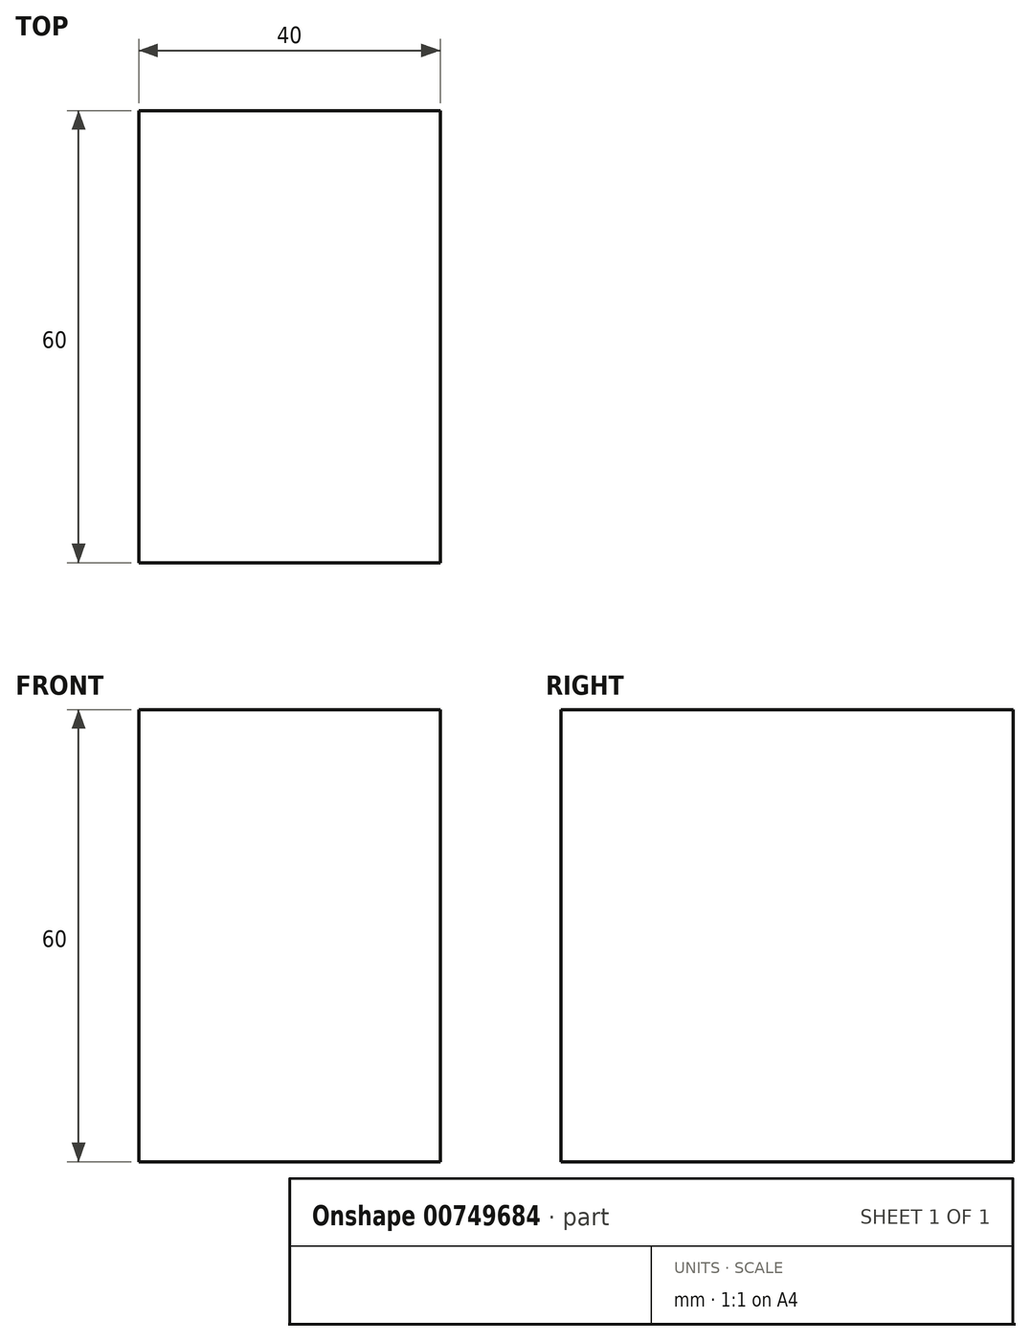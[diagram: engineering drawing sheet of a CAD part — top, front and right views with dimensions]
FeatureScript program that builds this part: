
annotation { "Feature Type Name" : "Feature", "Feature Type Description" : "" }
export const myFeature = defineFeature(function(context is Context, id is Id, definition is map)
    precondition{}
    {
        {
            var Q0;
            Q0=qCreatedBy(makeId("Front.planeOp"),FACE);
            var sketch = newSketch(context, id + "F0", { "sketchPlane" : qUnion([Q0])});
            skLineSegment(sketch, "E0", {"start": v(0, 0) * mm, "end": v(0, 60) * mm});
            skLineSegment(sketch, "E1", {"start": v(0, 60) * mm, "end": v(40, 60) * mm});
            skLineSegment(sketch, "E2", {"start": v(40, 60) * mm, "end": v(40, 0) * mm});
            skLineSegment(sketch, "E3", {"start": v(40, 0) * mm, "end": v(0, 0) * mm});
            skSolve(sketch);
        }
        {
            var Q0;
            Q0=makeQuery(id+"F0.imprint","IMPRINT",FACE,{"disambiguationData":[TD([[makeQuery(id+"F0.imprint","IMPRINT",EDGE,{"derivedFrom":sQuery(id+"F0.wireOp",EDGE,"E0")}),-1.0]])]});
            extrude(context, id + "F1", {"entities" : qUnion([Q0]), "depth" : 60 * mm, "offsetDistance" : 25 * mm});
        }
    });
